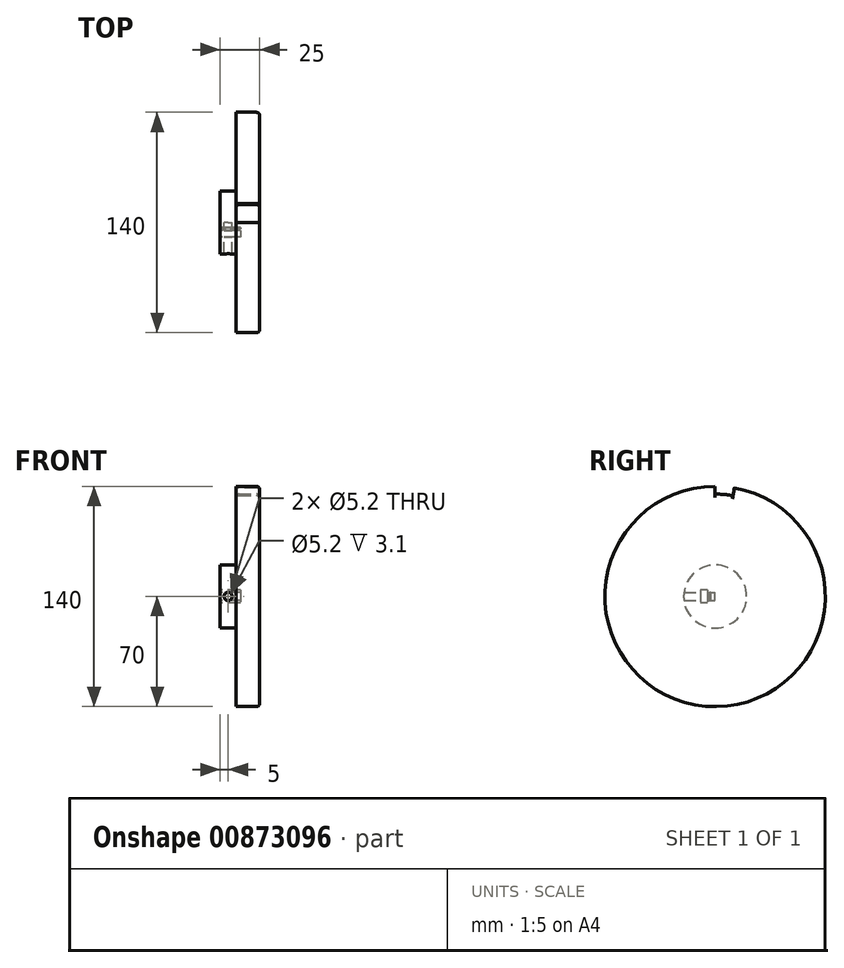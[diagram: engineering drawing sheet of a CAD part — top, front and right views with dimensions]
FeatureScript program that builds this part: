
annotation { "Feature Type Name" : "Feature", "Feature Type Description" : "" }
export const myFeature = defineFeature(function(context is Context, id is Id, definition is map)
    precondition{}
    {
        {
            var Q0;
            Q0=qCreatedBy(makeId("Right.planeOp"),FACE);
            var sketch = newSketch(context, id + "F0", { "sketchPlane" : qUnion([Q0])});
            skCircle(sketch, "E0", {"center": v(0, 0) * mm, "radius": 70 * mm});
            skSolve(sketch);
        }
        {
            var Q0;
            Q0 = qSketchRegion(id + "F0", true);
            extrude(context, id + "F1", {"entities" : qUnion([Q0]), "depth" : 25 * mm, "offsetDistance" : 25 * mm});
        }
        {
            var Q0;
            Q0=qCreatedBy(makeId("Right.planeOp"),FACE);
            var sketch = newSketch(context, id + "F2", { "sketchPlane" : qUnion([Q0])});
            skCircle(sketch, "E1", {"center": v(0, 0) * mm, "radius": 20 * mm});
            skCircle(sketch, "E2", {"center": v(0, 0) * mm, "radius": 70 * mm});
            skSolve(sketch);
        }
        {
            var Q0;
            Q0 = qSketchRegion(id + "F2", true);
            extrude(context, id + "F3", {"entities" : qUnion([Q0]), "operationType" : NewBodyOperationType.REMOVE, "depth" : 10 * mm, "offsetDistance" : 25 * mm});
        }
        {
            var Q0;
            Q0=qCreatedBy(makeId("Right.planeOp"),FACE);
            var sketch = newSketch(context, id + "F4", { "sketchPlane" : qUnion([Q0])});
            skCircle(sketch, "E3", {"center": v(0, 0) * mm, "radius": 60 * mm});
            skCircle(sketch, "E4", {"center": v(0, 0) * mm, "radius": 30 * mm});
            skLineSegment(sketch, "E5", {"start": v(0, 0) * mm, "end": v(60, 0) * mm});
            skLineSegment(sketch, "E6", {"start": v(0, 0) * mm, "end": v(49.15, -34.41) * mm});
            skSolve(sketch);
        }
        {
            var Q0;
            Q0=qCreatedBy(makeId("Front.planeOp"),FACE);
            var sketch = newSketch(context, id + "F5", { "sketchPlane" : qUnion([Q0])});
            skLineSegment(sketch, "E7.bottom", {"start": v(0, 0) * mm, "end": v(30, 0) * mm});
            skLineSegment(sketch, "E7.top", {"start": v(0, 80) * mm, "end": v(30, 80) * mm});
            skLineSegment(sketch, "E7.left", {"start": v(0, 0) * mm, "end": v(0, 80) * mm});
            skLineSegment(sketch, "E7.right", {"start": v(30, 0) * mm, "end": v(30, 80) * mm});
            skLineSegment(sketch, "E8", {"start": v(0, 65) * mm, "end": v(30, 65) * mm});
            skSolve(sketch);
        }
        {
            var Q0;
            {var subQ0=sQuery(id+"F5.wireOp",EDGE,"E7.top");Q0=makeQuery(id+"F5.imprint","IMPRINT",FACE,{"disambiguationData":[TD([[makeQuery(id+"F5.imprint","IMPRINT",EDGE,{"derivedFrom":subQ0}),-1.0]])]});}
            var Q1;
            Q1=sQuery(id+"F0.wireOp",EDGE,"E0");
            revolve(context, id + "F6", {"operationType" : NewBodyOperationType.REMOVE, "surfaceOperationType" : NewSurfaceOperationType.NEW, "entities" : qUnion([Q0]), "axis" : qUnion([Q1]), "revolveType" : RevolveType.ONE_DIRECTION, "oppositeDirection" : true, "angle" : 10 * degree});
        }
        {
            var Q0;
            {var subQ0=sQuery(id+"F0.wireOp",EDGE,"E0");var subQ2=sQuery(id+"F5.wireOp",EDGE,"E8");var subQ3=sQuery(id+"F5.wireOp",EDGE,"E7.right");var subQ4=sQuery(id+"F5.wireOp",EDGE,"E7.left");var subQ5=sQuery(id+"F5.wireOp",EDGE,"E7.top");var subQ7=makeQuery(id+"FpogJrtredL9Hyj_1.-19.F6.opRevolve","CAP_FACE",FACE,{"disambiguationData":[OSD([subQ5,subQ4,subQ3,subQ2])],"isStart":true});Q0=makeQuery(id+"FpogJrtredL9Hyj_1.-18.F6.boolean.opBoolean","SPLIT",EDGE,{"disambiguationData":[TD([makeQuery(id+"FpogJrtredL9Hyj_1.-19.F6.boolean.opBoolean","COPY",FACE,{"derivedFrom":subQ7})])],"derivedFrom":makeQuery(id+"FpogJrtredL9Hyj_1.-19.F6.boolean.opBoolean","SPLIT",EDGE,{"disambiguationData":[TD([makeQuery(id+"F6.boolean.opBoolean","COPY",FACE,{"derivedFrom":makeQuery(id+"F6.opRevolve","CAP_FACE",FACE,{"disambiguationData":[OSD([subQ5,subQ4,subQ3,subQ2])],"isStart":false})})])],"derivedFrom":makeQuery(id+"F1.opExtrude","CAP_EDGE",EDGE,{"disambiguationData":[OSD([subQ0])],"isStart":false})})});}
            var Q1;
            {var subQ1=sQuery(id+"F5.wireOp",EDGE,"E8");var subQ2=sQuery(id+"F5.wireOp",EDGE,"E7.right");var subQ3=sQuery(id+"F5.wireOp",EDGE,"E7.left");var subQ4=sQuery(id+"F5.wireOp",EDGE,"E7.top");var subQ5=sQuery(id+"F2.wireOp",EDGE,"E2");var subQ7=makeQuery(id+"FpogJrtredL9Hyj_1.-19.F6.opRevolve","CAP_FACE",FACE,{"disambiguationData":[OSD([subQ4,subQ3,subQ2,subQ1])],"isStart":true});Q1=makeQuery(id+"FpogJrtredL9Hyj_1.-18.F6.boolean.opBoolean","SPLIT",EDGE,{"disambiguationData":[TD([makeQuery(id+"FpogJrtredL9Hyj_1.-19.F6.boolean.opBoolean","COPY",FACE,{"derivedFrom":subQ7})])],"derivedFrom":makeQuery(id+"FpogJrtredL9Hyj_1.-19.F6.boolean.opBoolean","SPLIT",EDGE,{"disambiguationData":[TD([makeQuery(id+"F6.boolean.opBoolean","COPY",FACE,{"derivedFrom":makeQuery(id+"F6.opRevolve","CAP_FACE",FACE,{"disambiguationData":[OSD([subQ4,subQ3,subQ2,subQ1])],"isStart":false})})])],"derivedFrom":makeQuery(id+"F3.boolean.opBoolean","COPY",EDGE,{"derivedFrom":makeQuery(id+"F3.opExtrude","CAP_EDGE",EDGE,{"disambiguationData":[OSD([subQ5])],"isStart":false})})})});}
            var Q2;
            Q2=makeQuery(id+"F6.boolean.opBoolean","INTERSECT",EDGE,{"derivedFrom":[makeQuery(id+"F1.opExtrude","CAP_FACE",FACE,{"disambiguationData":[OSD([sQuery(id+"F0.wireOp",EDGE,"E0")])],"isStart":false}),makeQuery(id+"F6.opRevolve","SWEPT_FACE",FACE,{"disambiguationData":[OSD([sQuery(id+"F5.wireOp",EDGE,"E8")])]})]});
            var Q3;
            Q3=makeQuery(id+"F6.boolean.opBoolean","INTERSECT",EDGE,{"derivedFrom":[makeQuery(id+"F3.boolean.opBoolean","COPY",FACE,{"derivedFrom":makeQuery(id+"F3.opExtrude","CAP_FACE",FACE,{"disambiguationData":[OSD([sQuery(id+"F2.wireOp",EDGE,"E1"),sQuery(id+"F2.wireOp",EDGE,"E2")])],"isStart":false})}),makeQuery(id+"F6.opRevolve","SWEPT_FACE",FACE,{"disambiguationData":[OSD([sQuery(id+"F5.wireOp",EDGE,"E8")])]})]});
            fillet(context, id + "F7", {"entities" : qUnion([Q0, Q1, Q2, Q3]), "radius" : 2 * mm, "tangentPropagation" : true, "allowEdgeOverflow" : false});
        }
        {
            var Q0;
            Q0=qCreatedBy(makeId("Right.planeOp"),FACE);
            var sketch = newSketch(context, id + "F8", { "sketchPlane" : qUnion([Q0])});
            skCircle(sketch, "E9", {"center": v(0, 0) * mm, "radius": 4.1 * mm});
            skLineSegment(sketch, "E10.bottom", {"start": v(-3.1, 5) * mm, "end": v(-5.02, 5) * mm});
            skLineSegment(sketch, "E10.top", {"start": v(-3.1, -5) * mm, "end": v(-5.02, -5) * mm});
            skLineSegment(sketch, "E10.left", {"start": v(-5.02, 5) * mm, "end": v(-5.02, -5) * mm});
            skLineSegment(sketch, "E10.right", {"start": v(-3.1, 5) * mm, "end": v(-3.1, -5) * mm});
            skLineSegment(sketch, "E11.bottom", {"start": v(-5.02, 4.1) * mm, "end": v(-9.22, 4.1) * mm});
            skLineSegment(sketch, "E11.top", {"start": v(-5.02, -4.1) * mm, "end": v(-9.22, -4.1) * mm});
            skLineSegment(sketch, "E11.left", {"start": v(-5.02, 4.1) * mm, "end": v(-5.02, -4.1) * mm});
            skLineSegment(sketch, "E11.right", {"start": v(-9.22, 4.1) * mm, "end": v(-9.22, -4.1) * mm});
            skSolve(sketch);
        }
        {
            var Q0;
            Q0=makeQuery(id+"F8.imprint","IMPRINT",FACE,{"disambiguationData":[TD([[makeQuery(id+"F8.imprint","IMPRINT",EDGE,{"derivedFrom":sQuery(id+"F8.wireOp",EDGE,"E11.bottom")}),1.0]])]});
            var Q1;
            {var subQ0=sQuery(id+"F8.wireOp",EDGE,"E10.right");var subQ1=sQuery(id+"F8.wireOp",EDGE,"E9");var subQ2=makeQuery(id+"F8.imprint","INTERSECT",VERTEX,{"disambiguationData":[OD(0.0)],"derivedFrom":[subQ1,subQ0]});Q1=makeQuery(id+"F8.imprint","IMPRINT",FACE,{"disambiguationData":[TD([[makeQuery(id+"F8.imprint","IMPRINT",EDGE,{"disambiguationData":[TD([[subQ2,1.0]])],"derivedFrom":subQ1}),1.0]])]});}
            var Q2;
            Q2=sQuery(id+"F8.wireOp",EDGE,"E9");
            extrude(context, id + "F9", {"entities" : qUnion([Q0, Q1]), "operationType" : NewBodyOperationType.REMOVE, "surfaceEntities" : qUnion([Q2]), "depth" : 13 * mm, "offsetDistance" : 25 * mm});
        }
        {
            var Q0;
            Q0=qCreatedBy(makeId("Front.planeOp"),FACE);
            var sketch = newSketch(context, id + "F10", { "sketchPlane" : qUnion([Q0])});
            skCircle(sketch, "E12", {"center": v(5, 0) * mm, "radius": 2.6 * mm});
            skSolve(sketch);
        }
        {
            var Q0;
            Q0 = qSketchRegion(id + "F10", true);
            extrude(context, id + "F11", {"entities" : qUnion([Q0]), "operationType" : NewBodyOperationType.REMOVE, "oppositeDirection" : true, "depth" : 0 * mm, "offsetDistance" : 25 * mm, "hasSecondDirection" : true, "secondDirectionOppositeDirection" : false, "secondDirectionDepth" : 25 * mm});
        }
    });
